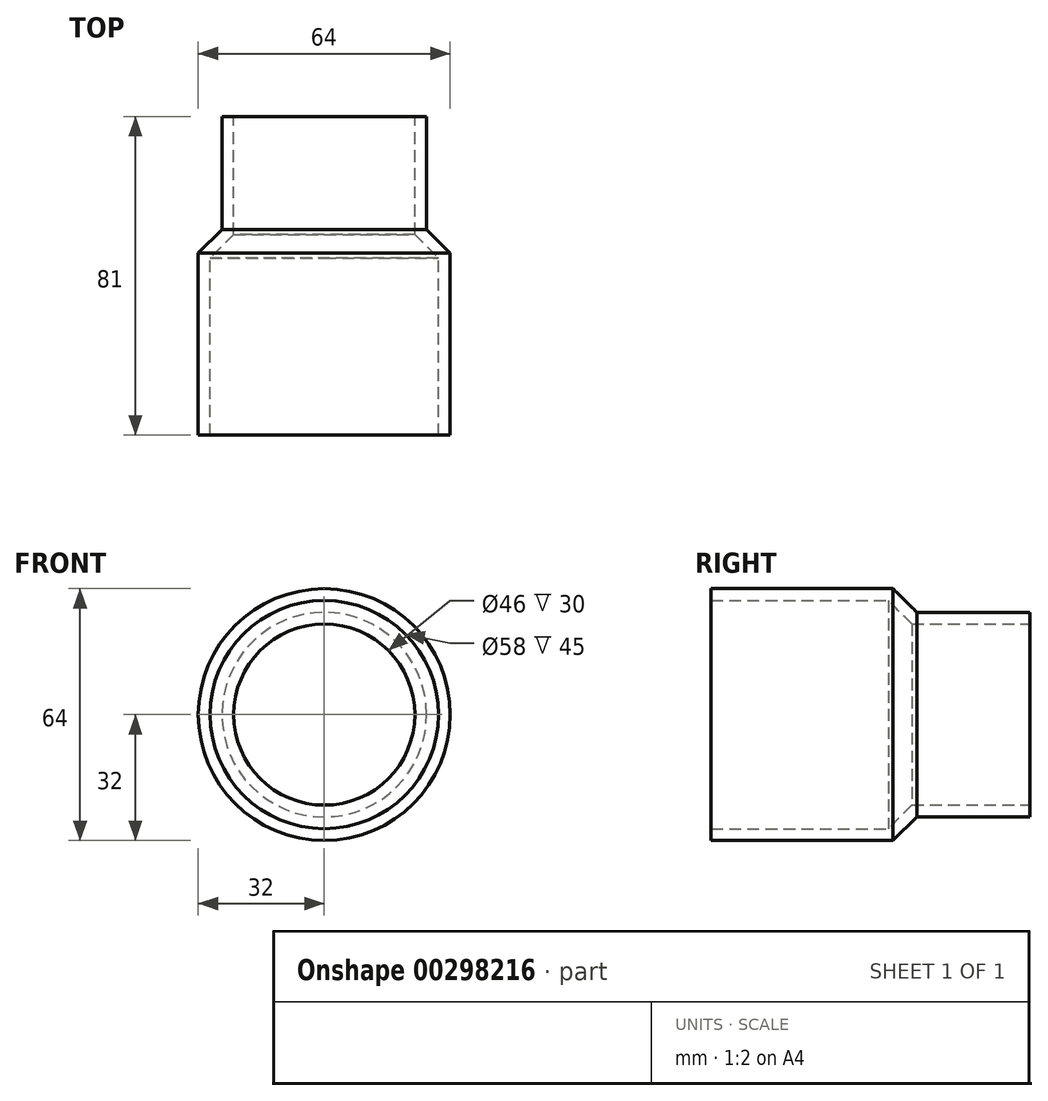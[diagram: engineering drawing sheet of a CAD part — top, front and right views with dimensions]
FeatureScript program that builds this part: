
annotation { "Feature Type Name" : "Feature", "Feature Type Description" : "" }
export const myFeature = defineFeature(function(context is Context, id is Id, definition is map)
    precondition{}
    {
        {
            var Q0;
            Q0=qCreatedBy(makeId("Top.planeOp"),FACE);
            var sketch = newSketch(context, id + "F0", { "sketchPlane" : qUnion([Q0])});
            skLineSegment(sketch, "E0", {"start": v(23, 0) * mm, "end": v(23, -30) * mm});
            skLineSegment(sketch, "E1", {"start": v(23, -30) * mm, "end": v(29, -36) * mm});
            skLineSegment(sketch, "E2", {"start": v(29, -36) * mm, "end": v(29, -81) * mm});
            skLineSegment(sketch, "E3.0", {"start": v(32, -34.76) * mm, "end": v(32, -81) * mm});
            skLineSegment(sketch, "E3.1", {"start": v(26, -28.76) * mm, "end": v(32, -34.76) * mm});
            skLineSegment(sketch, "E3.2", {"start": v(26, 0) * mm, "end": v(26, -28.76) * mm});
            skLineSegment(sketch, "E4", {"start": v(23, 0) * mm, "end": v(26, 0) * mm});
            skLineSegment(sketch, "E5", {"start": v(29, -81) * mm, "end": v(32, -81) * mm});
            skLineSegment(sketch, "E6", {"start": v(0, 0) * mm, "end": v(0, -74.97) * mm});
            skSolve(sketch);
        }
        {
            var Q0;
            Q0=makeQuery(id+"F0.imprint","IMPRINT",FACE,{"disambiguationData":[TD([[makeQuery(id+"F0.imprint","IMPRINT",EDGE,{"derivedFrom":sQuery(id+"F0.wireOp",EDGE,"E0")}),1.0]])]});
            var Q1;
            Q1=sQuery(id+"F0.wireOp",EDGE,"E6");
            revolve(context, id + "F1", {"entities" : qUnion([Q0]), "axis" : qUnion([Q1]), "revolveType" : RevolveType.FULL});
        }
    });
